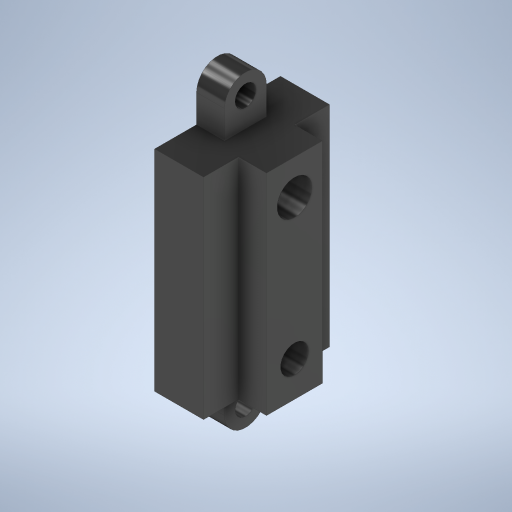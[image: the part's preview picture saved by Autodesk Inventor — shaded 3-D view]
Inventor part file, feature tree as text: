
AUTODESK INVENTOR PART (.ipt)
format: ipt  version: 2023 (Build 270158000, 158)  size: 297,984 bytes
history: native  units: mm
features: sketch x6, extrude x3, hole x3, mirror x1
ambient origin geometry x8: Origin, YZ Plane, XZ Plane, XY Plane, X Axis, Y Axis, Z Axis, Center Point
bodies: Volumenkörper1 (feature_tree)
feature tree (13):
  extrude  "Extrusion1"  Depth=18.0mm
  extrude  "Extrusion2"  Depth=8.0mm
  hole  "Bohrung1"  [1 undecoded]
  hole  "Bohrung2"  [1 undecoded]
  extrude  "Extrusion3"  Depth=10.0mm
  hole  "Bohrung3"  [1 undecoded]
  mirror  "Spiegeln1"
  sketch  "Skizze1"  dims[d0=30.0mm d1=18.0mm]
  sketch  "Skizze2"  dims[d2=7.0mm d3=0.0mm d4=8.0mm]
  sketch  "Skizze3"  dims[d5=30.0mm d6=4.0mm d7=0.0mm]
  sketch  "Skizze4"  dims[d8=5.0mm d9=6.0mm d10=4.0mm d11=2.0mm d12=90.0deg d13=4.0mm d14=20.594885mm]
  sketch  "Skizze5"  dims[d15=4.0mm d16=6.0mm d17=4.0mm d18=2.0mm d19=90.0deg d20=4.0mm d21=20.594885mm d22=0.0mm]
  sketch  "Skizze6"  dims[d23=5.0mm d24=10.0mm d25=4.0mm d26=90.0deg d27=3.0mm d28=3.0mm d29=4.0mm d30=0.0mm d31=3.0mm d32=6.0mm d33=4.0mm d34=2.0mm d35=90.0deg d36=4.0mm d37=20.594885mm d38=0.0mm]
note: 3 required parameter values undecoded (feature->parameter linkage not recoverable at this tier; creation-order binding heuristic only, values carry confidence <= 0.55)
